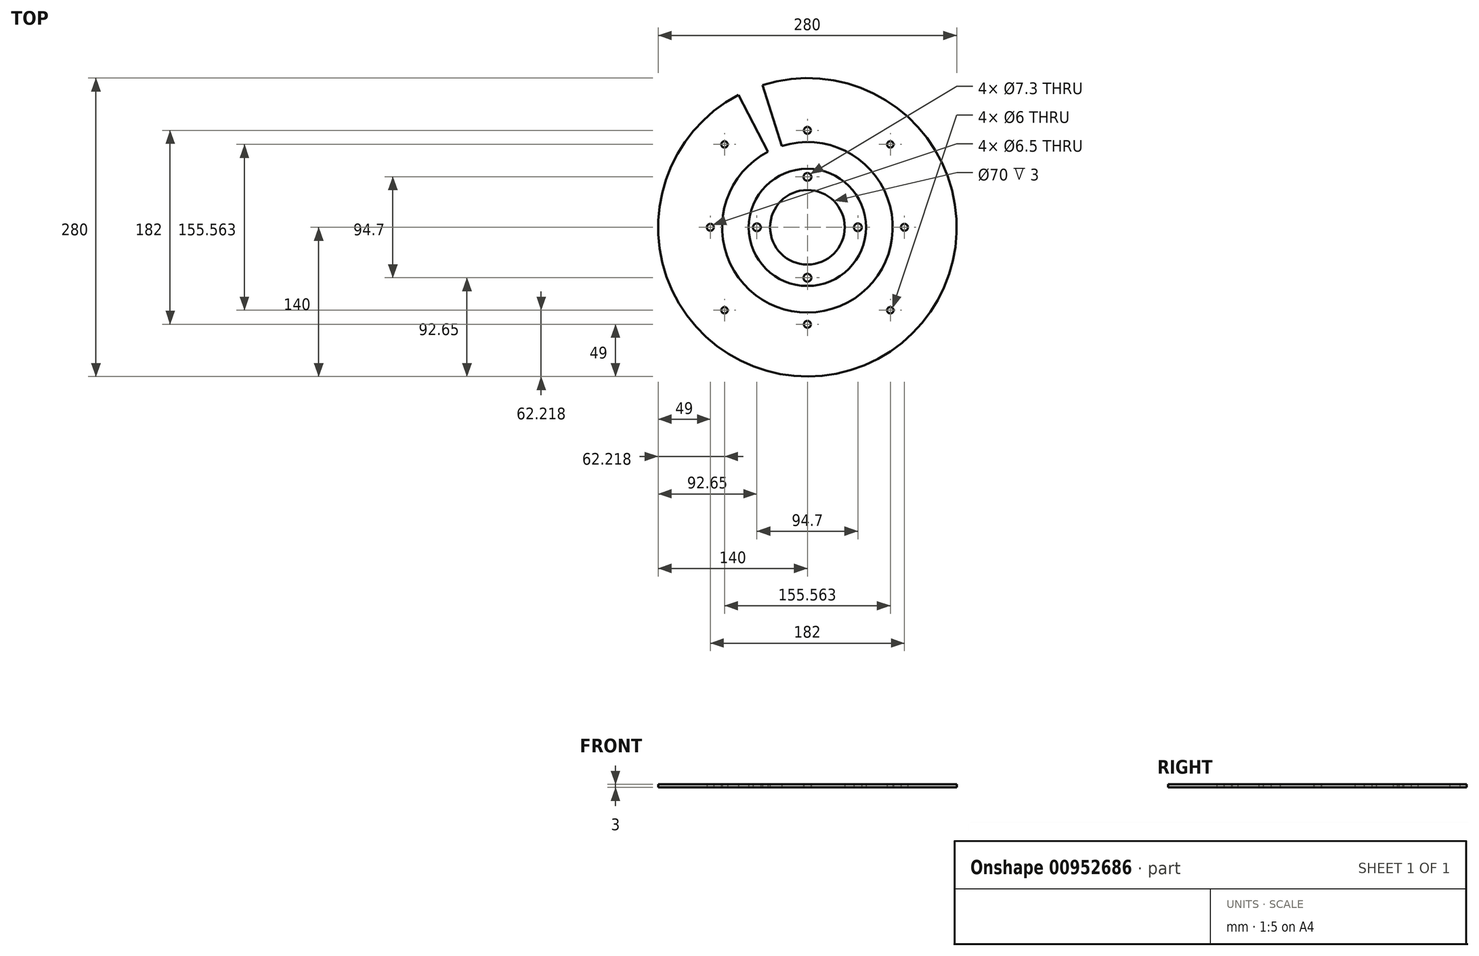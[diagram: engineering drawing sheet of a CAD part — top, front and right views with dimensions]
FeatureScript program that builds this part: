
annotation { "Feature Type Name" : "Feature", "Feature Type Description" : "" }
export const myFeature = defineFeature(function(context is Context, id is Id, definition is map)
    precondition{}
    {
        {
            var Q0;
            Q0=qCreatedBy(makeId("Top.planeOp"),FACE);
            var sketch = newSketch(context, id + "F0", { "sketchPlane" : qUnion([Q0])});
            skCircle(sketch, "E0", {"center": v(0, 0) * mm, "radius": 100 * mm, "construction": true});
            skCircle(sketch, "E1", {"center": v(0, 0) * mm, "radius": 80 * mm});
            skCircle(sketch, "E2", {"center": v(-91, 0) * mm, "radius": 3.25 * mm});
            skCircle(sketch, "E3", {"center": v(0, 0) * mm, "radius": 130 * mm, "construction": true});
            skCircle(sketch, "E4", {"center": v(-77.78, 77.78) * mm, "radius": 3 * mm});
            skLineSegment(sketch, "E5", {"start": v(-91, 0) * mm, "end": v(0, 0) * mm, "construction": true});
            skLineSegment(sketch, "E6", {"start": v(0, 0) * mm, "end": v(-77.78, 77.78) * mm, "construction": true});
            skCircle(sketch, "E7.1.0", {"center": v(0, -91) * mm, "radius": 3.25 * mm});
            skCircle(sketch, "E7.2.0", {"center": v(91, 0) * mm, "radius": 3.25 * mm});
            skCircle(sketch, "E7.3.0", {"center": v(0, 91) * mm, "radius": 3.25 * mm});
            skCircle(sketch, "E8.1.0", {"center": v(-77.78, -77.78) * mm, "radius": 3 * mm});
            skCircle(sketch, "E8.2.0", {"center": v(77.78, -77.78) * mm, "radius": 3 * mm});
            skCircle(sketch, "E8.3.0", {"center": v(77.78, 77.78) * mm, "radius": 3 * mm});
            skCircle(sketch, "E9", {"center": v(0, 0) * mm, "radius": 140 * mm});
            skLineSegment(sketch, "E10", {"start": v(-64.64, 124.18) * mm, "end": v(0, 0) * mm});
            skLineSegment(sketch, "E11", {"start": v(-42.1, 133.52) * mm, "end": v(0, 0) * mm});
            skCircle(sketch, "E12", {"center": v(0, 0) * mm, "radius": 35 * mm});
            skCircle(sketch, "E13", {"center": v(0, 0) * mm, "radius": 55 * mm});
            skCircle(sketch, "E14", {"center": v(0, 0) * mm, "radius": 47.35 * mm, "construction": true});
            skCircle(sketch, "E15", {"center": v(0, 47.35) * mm, "radius": 3.65 * mm});
            skCircle(sketch, "E16", {"center": v(-47.35, 0) * mm, "radius": 3.65 * mm});
            skCircle(sketch, "E17", {"center": v(0, -47.35) * mm, "radius": 3.65 * mm});
            skCircle(sketch, "E18", {"center": v(47.35, 0) * mm, "radius": 3.65 * mm});
            skSolve(sketch);
        }
        {
            var Q0;
            {var subQ0=sQuery(id+"F0.wireOp",EDGE,"E4");var subQ1=sQuery(id+"F0.wireOp",EDGE,"loMJ24n8-vsI0-bw0C-rTWu-dVK9hzXSYW2D");var subQ2=makeQuery(id+"F0.imprint","INTERSECT",VERTEX,{"disambiguationData":[OD(1.0)],"derivedFrom":[subQ1,subQ0]});Q0=makeQuery(id+"F0.imprint","IMPRINT",FACE,{"disambiguationData":[TD([[makeQuery(id+"F0.imprint","IMPRINT",EDGE,{"disambiguationData":[TD([[subQ2,-1.0]])],"derivedFrom":subQ1}),-1.0]])]});}
            var Q1;
            {var subQ0=sQuery(id+"F0.wireOp",EDGE,"E4");var subQ1=sQuery(id+"F0.wireOp",EDGE,"loMJ24n8-vsI0-bw0C-rTWu-dVK9hzXSYW2D");var subQ2=makeQuery(id+"F0.imprint","INTERSECT",VERTEX,{"disambiguationData":[OD(1.0)],"derivedFrom":[subQ1,subQ0]});Q1=makeQuery(id+"F0.imprint","IMPRINT",FACE,{"disambiguationData":[TD([[makeQuery(id+"F0.imprint","IMPRINT",EDGE,{"disambiguationData":[TD([[subQ2,-1.0]])],"derivedFrom":subQ1}),1.0]])]});}
            var Q2;
            {var subQ0=sQuery(id+"F0.wireOp",EDGE,"xdYz550y-TMS6-4Z2a-8SfC-K5T9KBGhguhw");var subQ1=sQuery(id+"F0.wireOp",EDGE,"E0");var subQ2=makeQuery(id+"F0.imprint","INTERSECT",VERTEX,{"derivedFrom":[subQ1,subQ0]});Q2=makeQuery(id+"F0.imprint","IMPRINT",FACE,{"disambiguationData":[TD([[makeQuery(id+"F0.imprint","IMPRINT",EDGE,{"disambiguationData":[TD([[subQ2,-1.0]])],"derivedFrom":subQ1}),-1.0]])]});}
            var Q3;
            {var subQ0=sQuery(id+"F0.wireOp",EDGE,"xdYz550y-TMS6-4Z2a-8SfC-K5T9KBGhguhw");var subQ1=sQuery(id+"F0.wireOp",EDGE,"E0");var subQ2=makeQuery(id+"F0.imprint","INTERSECT",VERTEX,{"derivedFrom":[subQ1,subQ0]});Q3=makeQuery(id+"F0.imprint","IMPRINT",FACE,{"disambiguationData":[TD([[makeQuery(id+"F0.imprint","IMPRINT",EDGE,{"disambiguationData":[TD([[subQ2,-1.0]])],"derivedFrom":subQ1}),1.0]])]});}
            var Q4;
            {var subQ0=sQuery(id+"F0.wireOp",EDGE,"xdYz550y-TMS6-4Z2a-8SfC-K5T9KBGhguhw");var subQ1=sQuery(id+"F0.wireOp",EDGE,"yUdectYR-K1RT-Pjwj-WCJF-mscGQmlpy0KV");var subQ2=makeQuery(id+"F0.imprint","INTERSECT",VERTEX,{"derivedFrom":[subQ1,subQ0]});Q4=makeQuery(id+"F0.imprint","IMPRINT",FACE,{"disambiguationData":[TD([[makeQuery(id+"F0.imprint","IMPRINT",EDGE,{"disambiguationData":[TD([[subQ2,-1.0]])],"derivedFrom":subQ1}),1.0]])]});}
            var Q5;
            {var subQ0=sQuery(id+"F0.wireOp",EDGE,"xdYz550y-TMS6-4Z2a-8SfC-K5T9KBGhguhw");var subQ1=sQuery(id+"F0.wireOp",EDGE,"eEvOi7P9-ZHYe-ZDzf-pxk9-3JI3EzQIZyuU");var subQ2=makeQuery(id+"F0.imprint","INTERSECT",VERTEX,{"derivedFrom":[subQ1,subQ0]});Q5=makeQuery(id+"F0.imprint","IMPRINT",FACE,{"disambiguationData":[TD([[makeQuery(id+"F0.imprint","IMPRINT",EDGE,{"disambiguationData":[TD([[subQ2,-1.0]])],"derivedFrom":subQ1}),-1.0]])]});}
            var Q6;
            {var subQ0=sQuery(id+"F0.wireOp",EDGE,"XClxmVRv-lAG1-IAUP-9N8M-4wk58tZdTk1G");var subQ1=sQuery(id+"F0.wireOp",EDGE,"eEvOi7P9-ZHYe-ZDzf-pxk9-3JI3EzQIZyuU");var subQ2=makeQuery(id+"F0.imprint","INTERSECT",VERTEX,{"derivedFrom":[subQ1,subQ0]});Q6=makeQuery(id+"F0.imprint","IMPRINT",FACE,{"disambiguationData":[TD([[makeQuery(id+"F0.imprint","IMPRINT",EDGE,{"disambiguationData":[TD([[subQ2,1.0]])],"derivedFrom":subQ1}),-1.0]])]});}
            var Q7;
            {var subQ0=sQuery(id+"F0.wireOp",EDGE,"XClxmVRv-lAG1-IAUP-9N8M-4wk58tZdTk1G");var subQ1=sQuery(id+"F0.wireOp",EDGE,"yUdectYR-K1RT-Pjwj-WCJF-mscGQmlpy0KV");var subQ2=makeQuery(id+"F0.imprint","INTERSECT",VERTEX,{"derivedFrom":[subQ1,subQ0]});Q7=makeQuery(id+"F0.imprint","IMPRINT",FACE,{"disambiguationData":[TD([[makeQuery(id+"F0.imprint","IMPRINT",EDGE,{"disambiguationData":[TD([[subQ2,1.0]])],"derivedFrom":subQ1}),1.0]])]});}
            var Q8;
            {var subQ0=sQuery(id+"F0.wireOp",EDGE,"XClxmVRv-lAG1-IAUP-9N8M-4wk58tZdTk1G");var subQ1=sQuery(id+"F0.wireOp",EDGE,"E0");var subQ2=makeQuery(id+"F0.imprint","INTERSECT",VERTEX,{"derivedFrom":[subQ1,subQ0]});Q8=makeQuery(id+"F0.imprint","IMPRINT",FACE,{"disambiguationData":[TD([[makeQuery(id+"F0.imprint","IMPRINT",EDGE,{"disambiguationData":[TD([[subQ2,1.0]])],"derivedFrom":subQ1}),1.0]])]});}
            var Q9;
            {var subQ0=sQuery(id+"F0.wireOp",EDGE,"XClxmVRv-lAG1-IAUP-9N8M-4wk58tZdTk1G");var subQ1=sQuery(id+"F0.wireOp",EDGE,"E0");var subQ2=makeQuery(id+"F0.imprint","INTERSECT",VERTEX,{"derivedFrom":[subQ1,subQ0]});Q9=makeQuery(id+"F0.imprint","IMPRINT",FACE,{"disambiguationData":[TD([[makeQuery(id+"F0.imprint","IMPRINT",EDGE,{"disambiguationData":[TD([[subQ2,1.0]])],"derivedFrom":subQ1}),-1.0]])]});}
            var Q10;
            {var subQ0=sQuery(id+"F0.wireOp",EDGE,"2bVxKzee-nFnR-5i7x-1aY8-o08pwLuBaxcQ");var subQ1=sQuery(id+"F0.wireOp",EDGE,"loMJ24n8-vsI0-bw0C-rTWu-dVK9hzXSYW2D");var subQ2=makeQuery(id+"F0.imprint","INTERSECT",VERTEX,{"disambiguationData":[OD(0.0)],"derivedFrom":[subQ1,subQ0]});Q10=makeQuery(id+"F0.imprint","IMPRINT",FACE,{"disambiguationData":[TD([[makeQuery(id+"F0.imprint","IMPRINT",EDGE,{"disambiguationData":[TD([[subQ2,1.0]])],"derivedFrom":subQ1}),1.0]])]});}
            var Q11;
            {var subQ0=sQuery(id+"F0.wireOp",EDGE,"2bVxKzee-nFnR-5i7x-1aY8-o08pwLuBaxcQ");var subQ1=sQuery(id+"F0.wireOp",EDGE,"loMJ24n8-vsI0-bw0C-rTWu-dVK9hzXSYW2D");var subQ2=makeQuery(id+"F0.imprint","INTERSECT",VERTEX,{"disambiguationData":[OD(0.0)],"derivedFrom":[subQ1,subQ0]});Q11=makeQuery(id+"F0.imprint","IMPRINT",FACE,{"disambiguationData":[TD([[makeQuery(id+"F0.imprint","IMPRINT",EDGE,{"disambiguationData":[TD([[subQ2,1.0]])],"derivedFrom":subQ1}),-1.0]])]});}
            var Q12;
            {var subQ0=sQuery(id+"F0.wireOp",EDGE,"JByOB8mt-SjlZ-skUg-WTkd-TIbIOLC4SLGQ");var subQ1=sQuery(id+"F0.wireOp",EDGE,"eEvOi7P9-ZHYe-ZDzf-pxk9-3JI3EzQIZyuU");var subQ2=makeQuery(id+"F0.imprint","INTERSECT",VERTEX,{"derivedFrom":[subQ1,subQ0]});Q12=makeQuery(id+"F0.imprint","IMPRINT",FACE,{"disambiguationData":[TD([[makeQuery(id+"F0.imprint","IMPRINT",EDGE,{"disambiguationData":[TD([[subQ2,-1.0]])],"derivedFrom":subQ1}),-1.0]])]});}
            var Q13;
            {var subQ0=sQuery(id+"F0.wireOp",EDGE,"JByOB8mt-SjlZ-skUg-WTkd-TIbIOLC4SLGQ");var subQ1=sQuery(id+"F0.wireOp",EDGE,"yUdectYR-K1RT-Pjwj-WCJF-mscGQmlpy0KV");var subQ2=makeQuery(id+"F0.imprint","INTERSECT",VERTEX,{"derivedFrom":[subQ1,subQ0]});Q13=makeQuery(id+"F0.imprint","IMPRINT",FACE,{"disambiguationData":[TD([[makeQuery(id+"F0.imprint","IMPRINT",EDGE,{"disambiguationData":[TD([[subQ2,-1.0]])],"derivedFrom":subQ1}),1.0]])]});}
            var Q14;
            {var subQ4=sQuery(id+"F0.wireOp",EDGE,"E0");var subQ6=sQuery(id+"F0.wireOp",EDGE,"xdYz550y-TMS6-4Z2a-8SfC-K5T9KBGhguhw");var subQ8=makeQuery(id+"F0.imprint","INTERSECT",VERTEX,{"derivedFrom":[subQ4,subQ6]});Q14=makeQuery(id+"F0.imprint","IMPRINT",FACE,{"disambiguationData":[TD([[makeQuery(id+"F0.imprint","IMPRINT",EDGE,{"disambiguationData":[TD([[subQ8,1.0]])],"derivedFrom":subQ4}),1.0]])]});}
            var Q15;
            {var subQ0=sQuery(id+"F0.wireOp",EDGE,"xdYz550y-TMS6-4Z2a-8SfC-K5T9KBGhguhw");var subQ1=sQuery(id+"F0.wireOp",EDGE,"E0");var subQ2=makeQuery(id+"F0.imprint","INTERSECT",VERTEX,{"derivedFrom":[subQ1,subQ0]});Q15=makeQuery(id+"F0.imprint","IMPRINT",FACE,{"disambiguationData":[TD([[makeQuery(id+"F0.imprint","IMPRINT",EDGE,{"disambiguationData":[TD([[subQ2,1.0]])],"derivedFrom":subQ1}),-1.0]])]});}
            var Q16;
            {var subQ0=sQuery(id+"F0.wireOp",EDGE,"2bVxKzee-nFnR-5i7x-1aY8-o08pwLuBaxcQ");var subQ1=sQuery(id+"F0.wireOp",EDGE,"loMJ24n8-vsI0-bw0C-rTWu-dVK9hzXSYW2D");var subQ2=makeQuery(id+"F0.imprint","INTERSECT",VERTEX,{"disambiguationData":[OD(1.0)],"derivedFrom":[subQ1,subQ0]});Q16=makeQuery(id+"F0.imprint","IMPRINT",FACE,{"disambiguationData":[TD([[makeQuery(id+"F0.imprint","IMPRINT",EDGE,{"disambiguationData":[TD([[subQ2,-1.0]])],"derivedFrom":subQ1}),1.0]])]});}
            var Q17;
            {var subQ0=sQuery(id+"F0.wireOp",EDGE,"2bVxKzee-nFnR-5i7x-1aY8-o08pwLuBaxcQ");var subQ1=sQuery(id+"F0.wireOp",EDGE,"loMJ24n8-vsI0-bw0C-rTWu-dVK9hzXSYW2D");var subQ2=makeQuery(id+"F0.imprint","INTERSECT",VERTEX,{"disambiguationData":[OD(1.0)],"derivedFrom":[subQ1,subQ0]});Q17=makeQuery(id+"F0.imprint","IMPRINT",FACE,{"disambiguationData":[TD([[makeQuery(id+"F0.imprint","IMPRINT",EDGE,{"disambiguationData":[TD([[subQ2,-1.0]])],"derivedFrom":subQ1}),-1.0]])]});}
            var Q18;
            {var subQ0=sQuery(id+"F0.wireOp",EDGE,"XClxmVRv-lAG1-IAUP-9N8M-4wk58tZdTk1G");var subQ1=sQuery(id+"F0.wireOp",EDGE,"yUdectYR-K1RT-Pjwj-WCJF-mscGQmlpy0KV");var subQ2=makeQuery(id+"F0.imprint","INTERSECT",VERTEX,{"derivedFrom":[subQ1,subQ0]});Q18=makeQuery(id+"F0.imprint","IMPRINT",FACE,{"disambiguationData":[TD([[makeQuery(id+"F0.imprint","IMPRINT",EDGE,{"disambiguationData":[TD([[subQ2,-1.0]])],"derivedFrom":subQ1}),1.0]])]});}
            var Q19;
            {var subQ0=sQuery(id+"F0.wireOp",EDGE,"XClxmVRv-lAG1-IAUP-9N8M-4wk58tZdTk1G");var subQ1=sQuery(id+"F0.wireOp",EDGE,"eEvOi7P9-ZHYe-ZDzf-pxk9-3JI3EzQIZyuU");var subQ2=makeQuery(id+"F0.imprint","INTERSECT",VERTEX,{"derivedFrom":[subQ1,subQ0]});Q19=makeQuery(id+"F0.imprint","IMPRINT",FACE,{"disambiguationData":[TD([[makeQuery(id+"F0.imprint","IMPRINT",EDGE,{"disambiguationData":[TD([[subQ2,-1.0]])],"derivedFrom":subQ1}),-1.0]])]});}
            var Q20;
            {var subQ0=sQuery(id+"F0.wireOp",EDGE,"PcUEsLnp-Eqhp-3JIy-qNyG-VJO0hjBXybVb");var subQ1=sQuery(id+"F0.wireOp",EDGE,"eEvOi7P9-ZHYe-ZDzf-pxk9-3JI3EzQIZyuU");var subQ2=makeQuery(id+"F0.imprint","INTERSECT",VERTEX,{"derivedFrom":[subQ1,subQ0]});Q20=makeQuery(id+"F0.imprint","IMPRINT",FACE,{"disambiguationData":[TD([[makeQuery(id+"F0.imprint","IMPRINT",EDGE,{"disambiguationData":[TD([[subQ2,1.0]])],"derivedFrom":subQ1}),-1.0]])]});}
            var Q21;
            {var subQ0=sQuery(id+"F0.wireOp",EDGE,"PcUEsLnp-Eqhp-3JIy-qNyG-VJO0hjBXybVb");var subQ1=sQuery(id+"F0.wireOp",EDGE,"yUdectYR-K1RT-Pjwj-WCJF-mscGQmlpy0KV");var subQ2=makeQuery(id+"F0.imprint","INTERSECT",VERTEX,{"derivedFrom":[subQ1,subQ0]});Q21=makeQuery(id+"F0.imprint","IMPRINT",FACE,{"disambiguationData":[TD([[makeQuery(id+"F0.imprint","IMPRINT",EDGE,{"disambiguationData":[TD([[subQ2,1.0]])],"derivedFrom":subQ1}),1.0]])]});}
            var Q22;
            {var subQ0=sQuery(id+"F0.wireOp",EDGE,"E2");var subQ1=sQuery(id+"F0.wireOp",EDGE,"yUdectYR-K1RT-Pjwj-WCJF-mscGQmlpy0KV");var subQ2=makeQuery(id+"F0.imprint","INTERSECT",VERTEX,{"derivedFrom":[subQ1,subQ0]});Q22=makeQuery(id+"F0.imprint","IMPRINT",FACE,{"disambiguationData":[TD([[makeQuery(id+"F0.imprint","IMPRINT",EDGE,{"disambiguationData":[TD([[subQ2,-1.0]])],"derivedFrom":subQ1}),1.0]])]});}
            var Q23;
            {var subQ0=sQuery(id+"F0.wireOp",EDGE,"E2");var subQ1=sQuery(id+"F0.wireOp",EDGE,"eEvOi7P9-ZHYe-ZDzf-pxk9-3JI3EzQIZyuU");var subQ2=makeQuery(id+"F0.imprint","INTERSECT",VERTEX,{"derivedFrom":[subQ1,subQ0]});Q23=makeQuery(id+"F0.imprint","IMPRINT",FACE,{"disambiguationData":[TD([[makeQuery(id+"F0.imprint","IMPRINT",EDGE,{"disambiguationData":[TD([[subQ2,-1.0]])],"derivedFrom":subQ1}),-1.0]])]});}
            var Q24;
            {var subQ0=sQuery(id+"F0.wireOp",EDGE,"DnK2NpJa-jMcF-HP5A-dMqR-ALW00YuRxGu1");var subQ1=sQuery(id+"F0.wireOp",EDGE,"loMJ24n8-vsI0-bw0C-rTWu-dVK9hzXSYW2D");var subQ2=makeQuery(id+"F0.imprint","INTERSECT",VERTEX,{"disambiguationData":[OD(1.0)],"derivedFrom":[subQ1,subQ0]});Q24=makeQuery(id+"F0.imprint","IMPRINT",FACE,{"disambiguationData":[TD([[makeQuery(id+"F0.imprint","IMPRINT",EDGE,{"disambiguationData":[TD([[subQ2,-1.0]])],"derivedFrom":subQ1}),-1.0]])]});}
            var Q25;
            {var subQ0=sQuery(id+"F0.wireOp",EDGE,"DnK2NpJa-jMcF-HP5A-dMqR-ALW00YuRxGu1");var subQ1=sQuery(id+"F0.wireOp",EDGE,"loMJ24n8-vsI0-bw0C-rTWu-dVK9hzXSYW2D");var subQ2=makeQuery(id+"F0.imprint","INTERSECT",VERTEX,{"disambiguationData":[OD(1.0)],"derivedFrom":[subQ1,subQ0]});Q25=makeQuery(id+"F0.imprint","IMPRINT",FACE,{"disambiguationData":[TD([[makeQuery(id+"F0.imprint","IMPRINT",EDGE,{"disambiguationData":[TD([[subQ2,-1.0]])],"derivedFrom":subQ1}),1.0]])]});}
            var Q26;
            {var subQ0=sQuery(id+"F0.wireOp",EDGE,"Ttljhc7K-EFSK-EuAQ-Vm9G-6Up0820TjMTI");var subQ1=sQuery(id+"F0.wireOp",EDGE,"E0");var subQ2=makeQuery(id+"F0.imprint","INTERSECT",VERTEX,{"derivedFrom":[subQ1,subQ0]});Q26=makeQuery(id+"F0.imprint","IMPRINT",FACE,{"disambiguationData":[TD([[makeQuery(id+"F0.imprint","IMPRINT",EDGE,{"disambiguationData":[TD([[subQ2,-1.0]])],"derivedFrom":subQ1}),-1.0]])]});}
            var Q27;
            {var subQ4=sQuery(id+"F0.wireOp",EDGE,"Ttljhc7K-EFSK-EuAQ-Vm9G-6Up0820TjMTI");var subQ5=sQuery(id+"F0.wireOp",EDGE,"E0");var subQ6=makeQuery(id+"F0.imprint","INTERSECT",VERTEX,{"derivedFrom":[subQ5,subQ4]});Q27=makeQuery(id+"F0.imprint","IMPRINT",FACE,{"disambiguationData":[TD([[makeQuery(id+"F0.imprint","IMPRINT",EDGE,{"disambiguationData":[TD([[subQ6,-1.0]])],"derivedFrom":subQ5}),1.0]])]});}
            var Q28;
            {var subQ0=sQuery(id+"F0.wireOp",EDGE,"Ttljhc7K-EFSK-EuAQ-Vm9G-6Up0820TjMTI");var subQ1=sQuery(id+"F0.wireOp",EDGE,"yUdectYR-K1RT-Pjwj-WCJF-mscGQmlpy0KV");var subQ2=makeQuery(id+"F0.imprint","INTERSECT",VERTEX,{"derivedFrom":[subQ1,subQ0]});Q28=makeQuery(id+"F0.imprint","IMPRINT",FACE,{"disambiguationData":[TD([[makeQuery(id+"F0.imprint","IMPRINT",EDGE,{"disambiguationData":[TD([[subQ2,-1.0]])],"derivedFrom":subQ1}),1.0]])]});}
            var Q29;
            {var subQ0=sQuery(id+"F0.wireOp",EDGE,"Ttljhc7K-EFSK-EuAQ-Vm9G-6Up0820TjMTI");var subQ1=sQuery(id+"F0.wireOp",EDGE,"eEvOi7P9-ZHYe-ZDzf-pxk9-3JI3EzQIZyuU");var subQ2=makeQuery(id+"F0.imprint","INTERSECT",VERTEX,{"derivedFrom":[subQ1,subQ0]});Q29=makeQuery(id+"F0.imprint","IMPRINT",FACE,{"disambiguationData":[TD([[makeQuery(id+"F0.imprint","IMPRINT",EDGE,{"disambiguationData":[TD([[subQ2,-1.0]])],"derivedFrom":subQ1}),-1.0]])]});}
            var Q30;
            {var subQ0=sQuery(id+"F0.wireOp",EDGE,"CDMablnw-Osua-2ARB-ImZD-hFvXebslcCEZ");var subQ1=sQuery(id+"F0.wireOp",EDGE,"yUdectYR-K1RT-Pjwj-WCJF-mscGQmlpy0KV");var subQ2=makeQuery(id+"F0.imprint","INTERSECT",VERTEX,{"derivedFrom":[subQ1,subQ0]});Q30=makeQuery(id+"F0.imprint","IMPRINT",FACE,{"disambiguationData":[TD([[makeQuery(id+"F0.imprint","IMPRINT",EDGE,{"disambiguationData":[TD([[subQ2,-1.0]])],"derivedFrom":subQ1}),1.0]])]});}
            var Q31;
            {var subQ0=sQuery(id+"F0.wireOp",EDGE,"CDMablnw-Osua-2ARB-ImZD-hFvXebslcCEZ");var subQ1=sQuery(id+"F0.wireOp",EDGE,"eEvOi7P9-ZHYe-ZDzf-pxk9-3JI3EzQIZyuU");var subQ2=makeQuery(id+"F0.imprint","INTERSECT",VERTEX,{"derivedFrom":[subQ1,subQ0]});Q31=makeQuery(id+"F0.imprint","IMPRINT",FACE,{"disambiguationData":[TD([[makeQuery(id+"F0.imprint","IMPRINT",EDGE,{"disambiguationData":[TD([[subQ2,-1.0]])],"derivedFrom":subQ1}),-1.0]])]});}
            var Q32;
            Q32=makeQuery(id+"F0.imprint","IMPRINT",FACE,{"disambiguationData":[TD([[makeQuery(id+"F0.imprint","IMPRINT",EDGE,{"derivedFrom":sQuery(id+"F0.wireOp",EDGE,"E2")}),-1.0]])]});
            extrude(context, id + "F1", {"entities" : qUnion([Q0, Q1, Q2, Q3, Q4, Q5, Q6, Q7, Q8, Q9, Q10, Q11, Q12, Q13, Q14, Q15, Q16, Q17, Q18, Q19, Q20, Q21, Q22, Q23, Q24, Q25, Q26, Q27, Q28, Q29, Q30, Q31, Q32]), "depth" : 3 * mm, "offsetDistance" : 25 * mm});
        }
        {
            var Q0;
            Q0=makeQuery(id+"F0.imprint","IMPRINT",FACE,{"disambiguationData":[TD([[makeQuery(id+"F0.imprint","IMPRINT",EDGE,{"derivedFrom":sQuery(id+"F0.wireOp",EDGE,"E15")}),-1.0]])]});
            var Q1;
            {var subQ0=sQuery(id+"F0.wireOp",EDGE,"E12");var subQ1=sQuery(id+"F0.wireOp",EDGE,"E10");var subQ2=makeQuery(id+"F0.imprint","INTERSECT",VERTEX,{"derivedFrom":[subQ1,subQ0]});Q1=makeQuery(id+"F0.imprint","IMPRINT",FACE,{"disambiguationData":[TD([[makeQuery(id+"F0.imprint","IMPRINT",EDGE,{"disambiguationData":[TD([[subQ2,1.0]])],"derivedFrom":subQ1}),1.0]])]});}
            extrude(context, id + "F2", {"entities" : qUnion([Q0, Q1]), "depth" : 3 * mm, "offsetDistance" : 25 * mm});
        }
    });
